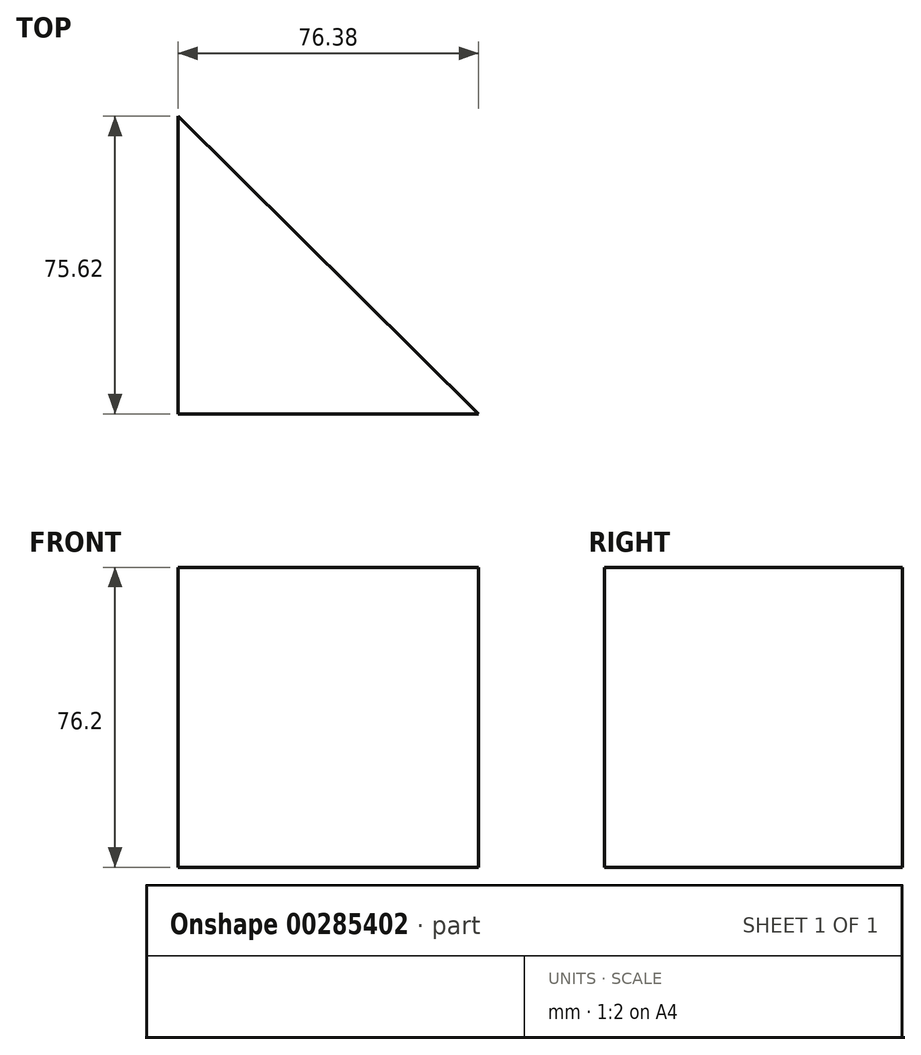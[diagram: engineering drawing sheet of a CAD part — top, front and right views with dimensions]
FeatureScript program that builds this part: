
annotation { "Feature Type Name" : "Feature", "Feature Type Description" : "" }
export const myFeature = defineFeature(function(context is Context, id is Id, definition is map)
    precondition{}
    {
        {
            var Q0;
            Q0=qCreatedBy(makeId("Top.planeOp"),FACE);
            var sketch = newSketch(context, id + "F0", { "sketchPlane" : qUnion([Q0])});
            skLineSegment(sketch, "E0.bottom", {"start": v(0, 0) * mm, "end": v(-76.38, 0) * mm});
            skLineSegment(sketch, "E0.top", {"start": v(0, 75.62) * mm, "end": v(-76.38, 75.62) * mm});
            skLineSegment(sketch, "E0.left", {"start": v(0, 0) * mm, "end": v(0, 75.62) * mm});
            skLineSegment(sketch, "E0.right", {"start": v(-76.38, 0) * mm, "end": v(-76.38, 75.62) * mm});
            skSolve(sketch);
        }
        {
            var Q0;
            Q0=qSketchRegion(id+"F0",true);
            extrude(context, id + "F1", {"entities" : qUnion([Q0]), "depth" : 76.2 * mm});
        }
        {
            var Q0;
            Q0=makeQuery(id+"F1.opExtrude","CAP_FACE",FACE,{"disambiguationData":[OSD([sQuery(id+"F0.wireOp",EDGE,"E0.bottom"),sQuery(id+"F0.wireOp",EDGE,"E0.top"),sQuery(id+"F0.wireOp",EDGE,"E0.left"),sQuery(id+"F0.wireOp",EDGE,"E0.right")])],"isStart":false});
            var sketch = newSketch(context, id + "F2", { "sketchPlane" : qUnion([Q0])});
            skLineSegment(sketch, "E1", {"start": v(-76.38, 75.62) * mm, "end": v(0, 0) * mm});
            skLineSegment(sketch, "E2", {"start": v(0, 0) * mm, "end": v(0, 75.62) * mm});
            skLineSegment(sketch, "E3", {"start": v(0, 75.62) * mm, "end": v(-76.38, 75.62) * mm});
            skSolve(sketch);
        }
        {
            var Q0;
            Q0=qSketchRegion(id+"F2",true);
            extrude(context, id + "F3", {"entities" : qUnion([Q0]), "operationType" : NewBodyOperationType.REMOVE, "oppositeDirection" : true, "depth" : 76.2 * mm});
        }
    });
